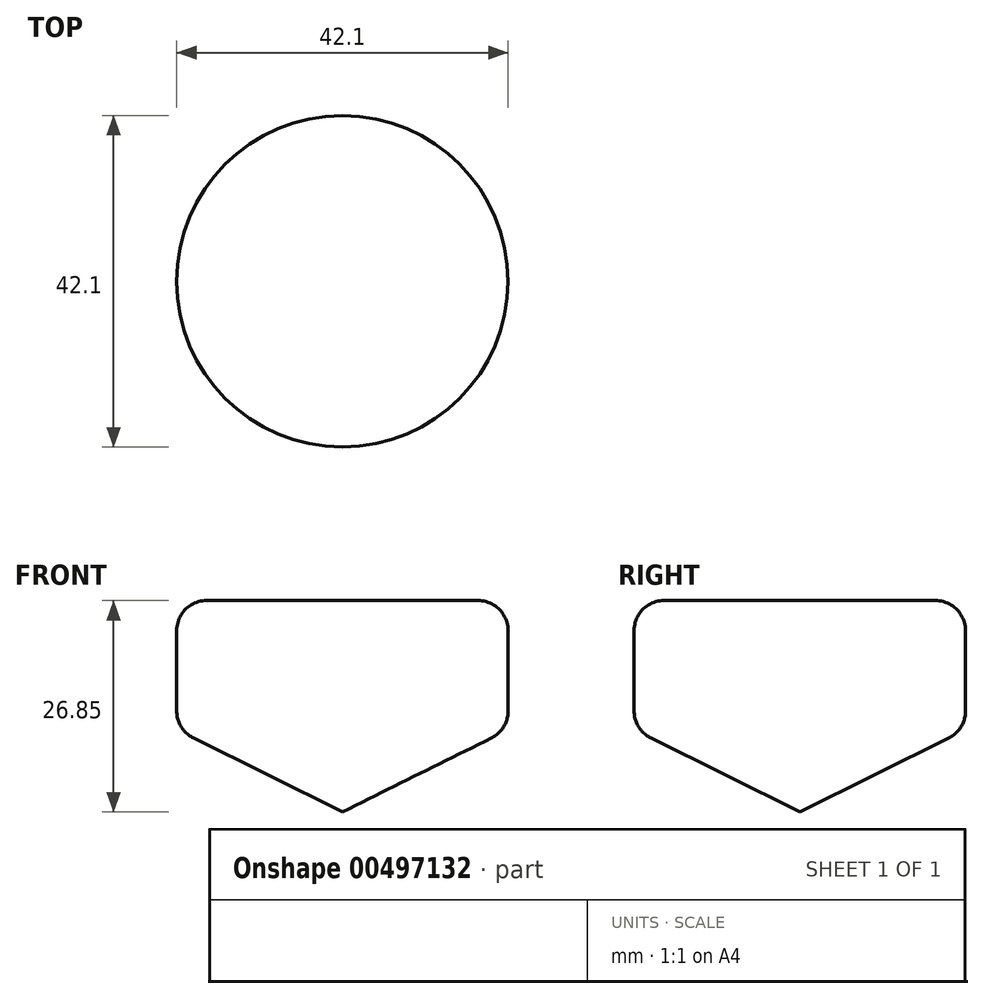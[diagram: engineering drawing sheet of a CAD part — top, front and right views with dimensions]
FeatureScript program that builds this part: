
annotation { "Feature Type Name" : "Feature", "Feature Type Description" : "" }
export const myFeature = defineFeature(function(context is Context, id is Id, definition is map)
    precondition{}
    {
        {
            var Q0;
            Q0=qCreatedBy(makeId("Front.planeOp"),FACE);
            var sketch = newSketch(context, id + "F0", { "sketchPlane" : qUnion([Q0])});
            skLineSegment(sketch, "E0", {"start": v(0, 0) * mm, "end": v(18.93, 9.38) * mm});
            skLineSegment(sketch, "E1", {"start": v(21.05, 23.04) * mm, "end": v(21.05, 12.8) * mm});
            skLineSegment(sketch, "E2", {"start": v(17.24, 26.85) * mm, "end": v(0, 26.85) * mm});
            skLineSegment(sketch, "E3", {"start": v(0, 26.85) * mm, "end": v(0, 0) * mm});
            skPoint(sketch, "E4.visualSharp", {"position": v(21.05, 26.85) * mm});
            skArc(sketch, "E4.filletArc", {"start": v(21.05, 23.04) * mm, "mid": v(19.93, 25.73) * mm, "end": v(17.24, 26.85) * mm});
            skPoint(sketch, "E5.visualSharp", {"position": v(21.05, 10.43) * mm});
            skArc(sketch, "E5.filletArc", {"start": v(18.93, 9.38) * mm, "mid": v(20.47, 10.78) * mm, "end": v(21.05, 12.8) * mm});
            skSolve(sketch);
        }
        {
            var Q0;
            Q0 = qSketchRegion(id + "F0", true);
            var Q1;
            Q1=sQuery(id+"F0.wireOp",EDGE,"E3");
            revolve(context, id + "F1", {"entities" : qUnion([Q0]), "axis" : qUnion([Q1]), "revolveType" : RevolveType.FULL});
        }
    });
